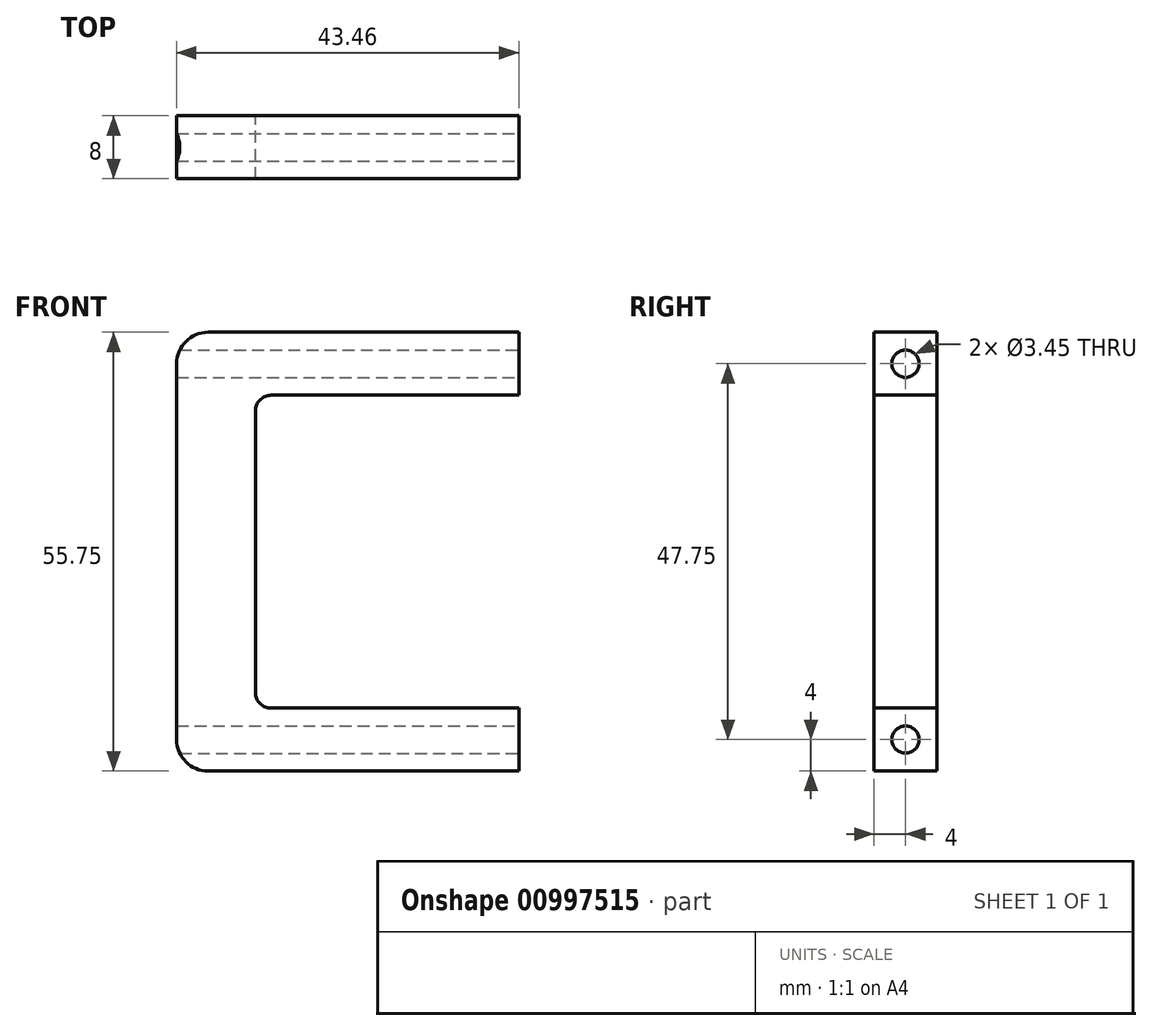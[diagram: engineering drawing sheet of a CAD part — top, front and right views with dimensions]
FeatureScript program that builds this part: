
annotation { "Feature Type Name" : "Feature", "Feature Type Description" : "" }
export const myFeature = defineFeature(function(context is Context, id is Id, definition is map)
    precondition{}
    {
        {
            var Q0;
            Q0=qCreatedBy(makeId("Front.planeOp"),FACE);
            var sketch = newSketch(context, id + "F0", { "sketchPlane" : qUnion([Q0])});
            skLineSegment(sketch, "E0.bottom", {"start": v(0, 0) * mm, "end": v(-12, 0) * mm});
            skLineSegment(sketch, "E0.top", {"start": v(0, -23.15) * mm, "end": v(-2.15, -23.15) * mm});
            skLineSegment(sketch, "E0.left", {"start": v(0, 0) * mm, "end": v(0, -23.15) * mm});
            skLineSegment(sketch, "E0.right", {"start": v(-12, 0) * mm, "end": v(-12, -4.85) * mm});
            skLineSegment(sketch, "E1.bottom", {"start": v(-29.46, -35.75) * mm, "end": v(-2.15, -35.75) * mm});
            skLineSegment(sketch, "E1.top", {"start": v(-29.46, -4.85) * mm, "end": v(-12, -4.85) * mm});
            skLineSegment(sketch, "E1.left", {"start": v(-29.46, -35.75) * mm, "end": v(-29.46, -4.85) * mm});
            skLineSegment(sketch, "E1.right", {"start": v(-2.15, -35.75) * mm, "end": v(-2.15, -23.15) * mm});
            skSolve(sketch);
        }
        {
            var Q0;
            Q0=qCreatedBy(makeId("Front.planeOp"),FACE);
            var sketch = newSketch(context, id + "F1", { "sketchPlane" : qUnion([Q0])});
            skLineSegment(sketch, "E2.bottom", {"start": v(0, 0) * mm, "end": v(-31.46, 0) * mm});
            skLineSegment(sketch, "E2.top", {"start": v(0, 8) * mm, "end": v(-39.46, 8) * mm});
            skLineSegment(sketch, "E2.left", {"start": v(0, 0) * mm, "end": v(0, 8) * mm});
            skLineSegment(sketch, "E2.right", {"start": v(-43.46, 0) * mm, "end": v(-43.46, 4) * mm});
            skLineSegment(sketch, "E3.top", {"start": v(-33.46, -47.75) * mm, "end": v(-39.46, -47.75) * mm});
            skLineSegment(sketch, "E3.left", {"start": v(-33.46, -2) * mm, "end": v(-33.46, -37.75) * mm});
            skLineSegment(sketch, "E3.right", {"start": v(-43.46, 0) * mm, "end": v(-43.46, -43.75) * mm});
            skLineSegment(sketch, "E4.bottom", {"start": v(-31.46, -39.75) * mm, "end": v(0, -39.75) * mm});
            skLineSegment(sketch, "E4.top", {"start": v(-33.46, -47.75) * mm, "end": v(0, -47.75) * mm});
            skLineSegment(sketch, "E4.right", {"start": v(0, -39.75) * mm, "end": v(0, -47.75) * mm});
            skPoint(sketch, "E5.visualSharp", {"position": v(-33.46, 0) * mm});
            skArc(sketch, "E5.filletArc", {"start": v(-31.46, 0) * mm, "mid": v(-32.87, -0.59) * mm, "end": v(-33.46, -2) * mm});
            skPoint(sketch, "E6.visualSharp", {"position": v(-43.46, 8) * mm});
            skArc(sketch, "E6.filletArc", {"start": v(-39.46, 8) * mm, "mid": v(-42.29, 6.83) * mm, "end": v(-43.46, 4) * mm});
            skPoint(sketch, "E7.visualSharp", {"position": v(-43.46, -47.75) * mm});
            skArc(sketch, "E7.filletArc", {"start": v(-43.46, -43.75) * mm, "mid": v(-42.29, -46.58) * mm, "end": v(-39.46, -47.75) * mm});
            skPoint(sketch, "E8.visualSharp", {"position": v(-33.46, -39.75) * mm});
            skArc(sketch, "E8.filletArc", {"start": v(-33.46, -37.75) * mm, "mid": v(-32.87, -39.16) * mm, "end": v(-31.46, -39.75) * mm});
            skSolve(sketch);
        }
        {
            var Q0;
            Q0=makeQuery(id+"F1.imprint","IMPRINT",FACE,{"disambiguationData":[TD([[makeQuery(id+"F1.imprint","IMPRINT",EDGE,{"derivedFrom":sQuery(id+"F1.wireOp",EDGE,"E2.bottom")}),-1.0]])]});
            extrude(context, id + "F2", {"entities" : qUnion([Q0]), "depth" : 8 * mm, "offsetDistance" : 25 * mm});
        }
        {
            var Q0;
            Q0=makeQuery(id+"F2.opExtrude","SWEPT_FACE",FACE,{"disambiguationData":[OSD([sQuery(id+"F1.wireOp",EDGE,"E2.left")])]});
            var sketch = newSketch(context, id + "F3", { "sketchPlane" : qUnion([Q0])});
            skPoint(sketch, "E9", {"position": v(-4, 4) * mm});
            skPoint(sketch, "E9.positionSnap0", {"position": v(-8, 4) * mm});
            skPoint(sketch, "E10", {"position": v(-4, -43.75) * mm});
            skSolve(sketch);
        }
        {
            var Q0;
            Q0=sQuery(id+"F3.wireOp",VERTEX,"E9");
            var Q1;
            Q1=sQuery(id+"F3.wireOp",VERTEX,"E10");
            var Q2;
            Q2=makeQuery(id+"F2.opExtrude","SWEPT_BODY",BODY,{"disambiguationData":[OSD([sQuery(id+"F1.wireOp",EDGE,"E2.bottom"),sQuery(id+"F1.wireOp",EDGE,"E2.top"),sQuery(id+"F1.wireOp",EDGE,"E2.left"),sQuery(id+"F1.wireOp",EDGE,"E2.right"),sQuery(id+"F1.wireOp",EDGE,"E3.top"),sQuery(id+"F1.wireOp",EDGE,"E3.left"),sQuery(id+"F1.wireOp",EDGE,"E3.right"),sQuery(id+"F1.wireOp",EDGE,"E4.bottom"),sQuery(id+"F1.wireOp",EDGE,"E4.top"),sQuery(id+"F1.wireOp",EDGE,"E4.right"),sQuery(id+"F1.wireOp",EDGE,"E5.filletArc"),sQuery(id+"F1.wireOp",EDGE,"E6.filletArc"),sQuery(id+"F1.wireOp",EDGE,"E7.filletArc"),sQuery(id+"F1.wireOp",EDGE,"E8.filletArc")])]});
            hole(context, id + "F4", {"style" : HoleStyle.SIMPLE, "endStyle" : HoleEndStyle.THROUGH, "standardTappedOrClearance" : lookupTablePath({ "standard" : "ANSI", "engagement" : "75%", "pitch" : "32 tpi", "size" : "#8", "type" : "Tapped" }), "standardBlindInLast" : lookupTablePath({ "standard" : "ANSI", "fit" : "Normal", "engagement" : "75%", "pitch" : "32 tpi", "size" : "#8", "type" : "Clearance & tapped" }), "holeDiameter" : 3.45 * mm, "majorDiameter" : 4.17 * mm, "showTappedDepth" : true, "isTappedThrough" : true, "tappedDepth" : 12 * mm, "tapClearance" : 3, "locations" : qUnion([Q0, Q1]), "scope" : qUnion([Q2])});
        }
    });
